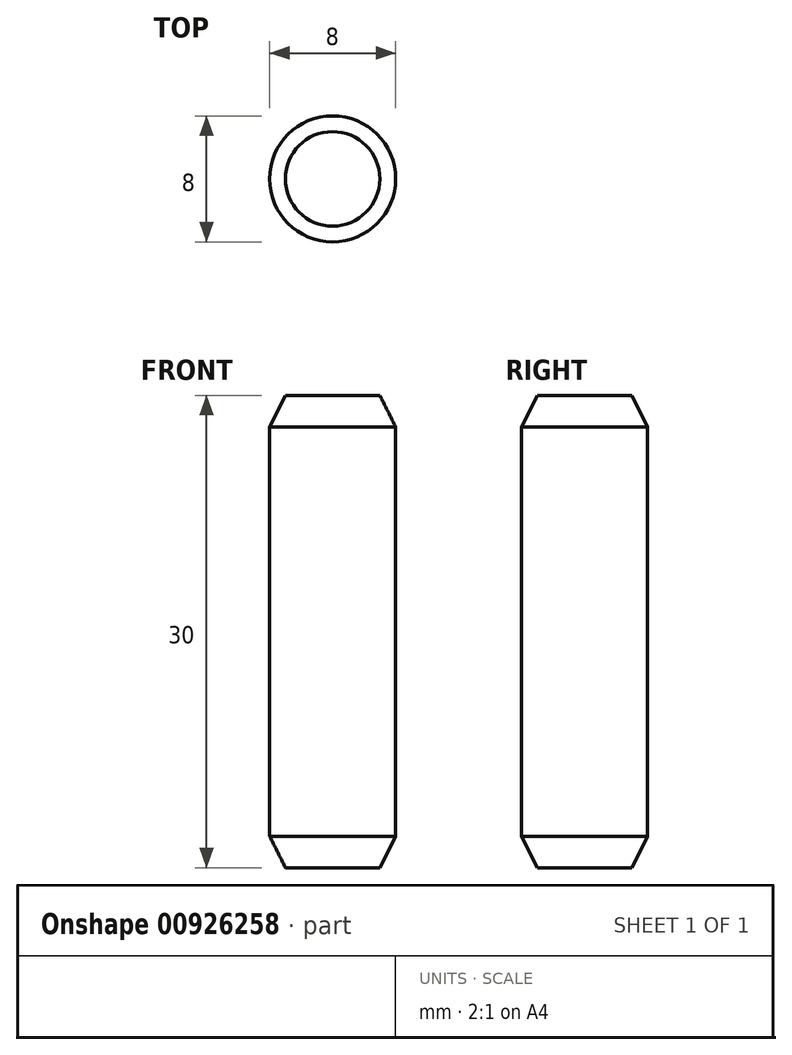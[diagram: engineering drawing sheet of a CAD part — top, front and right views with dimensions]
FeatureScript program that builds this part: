
annotation { "Feature Type Name" : "Feature", "Feature Type Description" : "" }
export const myFeature = defineFeature(function(context is Context, id is Id, definition is map)
    precondition{}
    {
        {
            var Q0;
            Q0=qCreatedBy(makeId("Front.planeOp"),FACE);
            var sketch = newSketch(context, id + "F0", { "sketchPlane" : qUnion([Q0])});
            skPoint(sketch, "E0.middle", {"position": v(0, 0) * mm});
            skLineSegment(sketch, "E1", {"start": v(0, 0) * mm, "end": v(0, 45) * mm, "construction": true});
            skLineSegment(sketch, "E2", {"start": v(0, 0) * mm, "end": v(-4, 0) * mm});
            skLineSegment(sketch, "E3", {"start": v(-4, 0) * mm, "end": v(-4, 30) * mm});
            skLineSegment(sketch, "E4", {"start": v(-4, 30) * mm, "end": v(0, 30) * mm});
            skLineSegment(sketch, "E5", {"start": v(0, 30) * mm, "end": v(0, 0) * mm});
            skSolve(sketch);
        }
        {
            var Q0;
            Q0=makeQuery(id+"F0.imprint","IMPRINT",FACE,{"disambiguationData":[TD([[makeQuery(id+"F0.imprint","IMPRINT",EDGE,{"derivedFrom":sQuery(id+"F0.wireOp",EDGE,"E2")}),-1.0]])]});
            var Q1;
            Q1=sQuery(id+"F0.wireOp",EDGE,"E1");
            revolve(context, id + "F1", {"surfaceOperationType" : NewSurfaceOperationType.NEW, "entities" : qUnion([Q0]), "axis" : qUnion([Q1]), "revolveType" : RevolveType.FULL});
        }
        {
            var Q0;
            Q0=makeQuery(id+"F1.opRevolve","SWEPT_EDGE",EDGE,{"disambiguationData":[OSD([sQuery(id+"F0.wireOp",EDGE,"E3"),sQuery(id+"F0.wireOp",EDGE,"E4")])]});
            chamfer(context, id + "F2", {"entities" : qUnion([Q0]), "chamferType" : ChamferType.TWO_OFFSETS, "width1" : 2 * mm, "oppositeDirection" : false, "width2" : 1 * mm, "tangentPropagation" : true});
        }
        {
            var Q0;
            Q0=makeQuery(id+"F1.opRevolve","SWEPT_EDGE",EDGE,{"disambiguationData":[OSD([sQuery(id+"F0.wireOp",EDGE,"E2"),sQuery(id+"F0.wireOp",EDGE,"E3")])]});
            chamfer(context, id + "F3", {"entities" : qUnion([Q0]), "chamferType" : ChamferType.TWO_OFFSETS, "width1" : 1 * mm, "oppositeDirection" : false, "width2" : 2 * mm, "tangentPropagation" : true});
        }
    });
